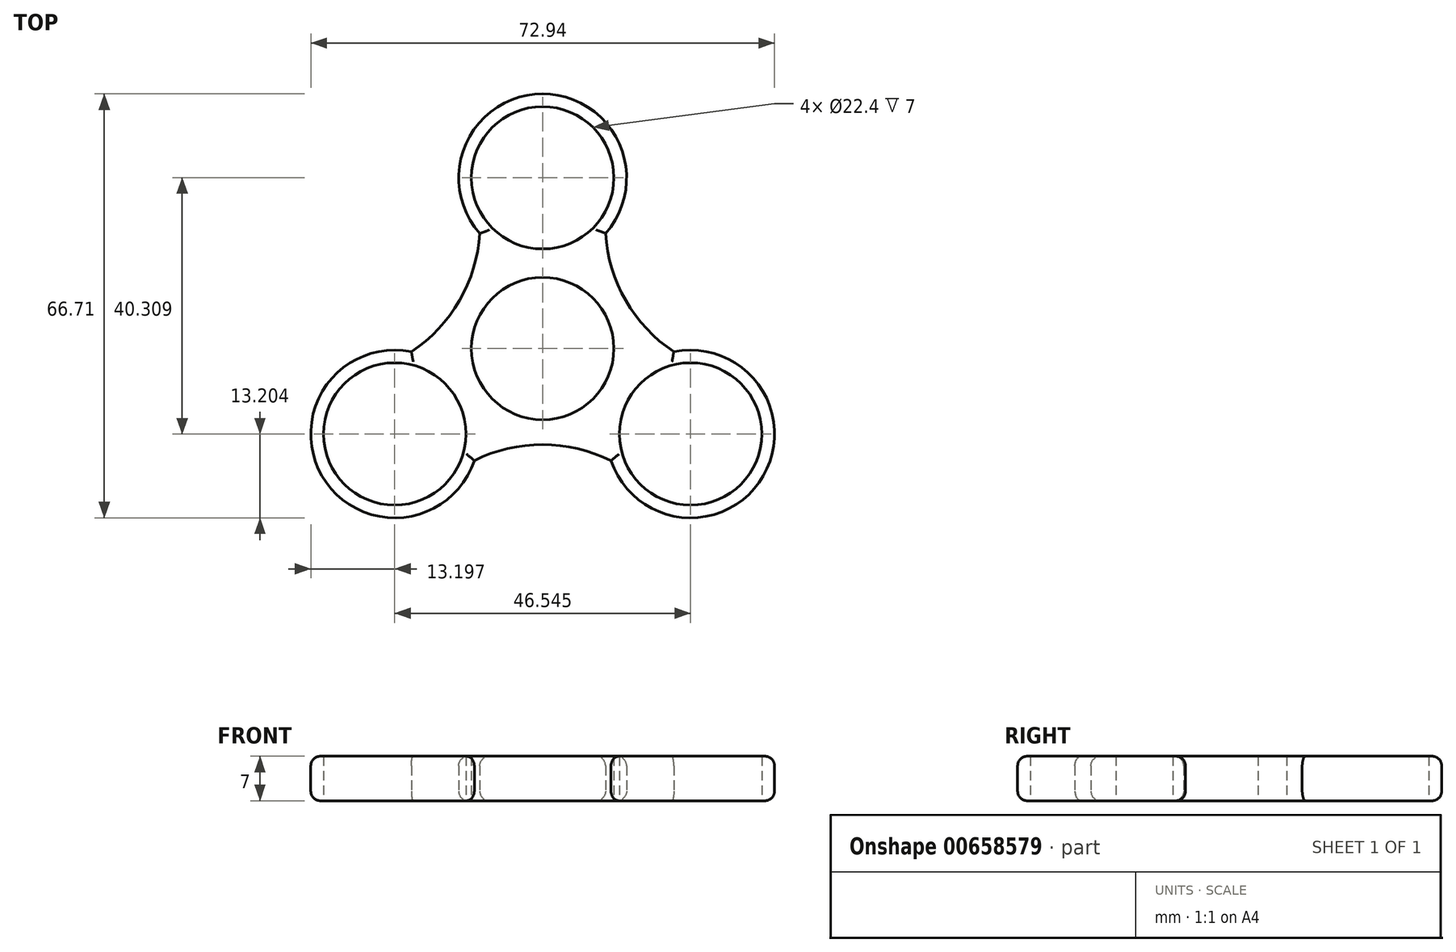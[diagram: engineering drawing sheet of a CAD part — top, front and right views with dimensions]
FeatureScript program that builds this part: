
annotation { "Feature Type Name" : "Feature", "Feature Type Description" : "" }
export const myFeature = defineFeature(function(context is Context, id is Id, definition is map)
    precondition{}
    {
        {
            var Q0;
            Q0=qCreatedBy(makeId("Top.planeOp"),FACE);
            var sketch = newSketch(context, id + "F0", { "sketchPlane" : qUnion([Q0])});
            skCircle(sketch, "E0", {"center": v(0, 0) * mm, "radius": 11.2 * mm});
            skCircle(sketch, "E1", {"center": v(0, 26.87) * mm, "radius": 11.2 * mm});
            skArc(sketch, "E2", {"start": v(9.9, 18.13) * mm, "mid": v(0, 40.07) * mm, "end": v(-9.88, 18.12) * mm});
            skArc(sketch, "E3.1.0", {"start": v(-20.65, -0.5) * mm, "mid": v(-34.7, -20.04) * mm, "end": v(-10.75, -17.62) * mm});
            skCircle(sketch, "E3.1.1", {"center": v(-23.27, -13.44) * mm, "radius": 11.2 * mm});
            skArc(sketch, "E3.2.0", {"start": v(10.76, -17.64) * mm, "mid": v(34.7, -20.03) * mm, "end": v(20.64, -0.5) * mm});
            skCircle(sketch, "E3.2.1", {"center": v(23.27, -13.44) * mm, "radius": 11.2 * mm});
            skArc(sketch, "E4", {"start": v(9.9, 18.13) * mm, "mid": v(13.08, 7.56) * mm, "end": v(20.64, -0.5) * mm});
            skArc(sketch, "E5.1.0", {"start": v(-20.65, -0.5) * mm, "mid": v(-13.08, 7.55) * mm, "end": v(-9.88, 18.12) * mm});
            skArc(sketch, "E5.2.0", {"start": v(10.76, -17.64) * mm, "mid": v(0, -15.1) * mm, "end": v(-10.75, -17.62) * mm});
            skSolve(sketch);
        }
        {
            var Q0;
            Q0=makeQuery(id+"F0.imprint","IMPRINT",FACE,{"disambiguationData":[TD([[makeQuery(id+"F0.imprint","IMPRINT",EDGE,{"derivedFrom":sQuery(id+"F0.wireOp",EDGE,"E0")}),-1.0]])]});
            extrude(context, id + "F1", {"entities" : qUnion([Q0]), "depth" : 7 * mm, "offsetDistance" : 25 * mm});
        }
        {
            var Q0;
            Q0=makeQuery(id+"F1.opExtrude","CAP_EDGE",EDGE,{"disambiguationData":[OSD([sQuery(id+"F0.wireOp",EDGE,"E3.1.0")])],"isStart":false});
            var Q1;
            Q1=makeQuery(id+"F1.opExtrude","CAP_EDGE",EDGE,{"disambiguationData":[OSD([sQuery(id+"F0.wireOp",EDGE,"E5.1.0")])],"isStart":false});
            var Q2;
            Q2=makeQuery(id+"F1.opExtrude","CAP_EDGE",EDGE,{"disambiguationData":[OSD([sQuery(id+"F0.wireOp",EDGE,"E4")])],"isStart":false});
            var Q3;
            Q3=makeQuery(id+"F1.opExtrude","CAP_EDGE",EDGE,{"disambiguationData":[OSD([sQuery(id+"F0.wireOp",EDGE,"E5.2.0")])],"isStart":false});
            var Q4;
            Q4=makeQuery(id+"F1.opExtrude","CAP_EDGE",EDGE,{"disambiguationData":[OSD([sQuery(id+"F0.wireOp",EDGE,"E3.2.0")])],"isStart":false});
            var Q5;
            Q5=makeQuery(id+"F1.opExtrude","CAP_EDGE",EDGE,{"disambiguationData":[OSD([sQuery(id+"F0.wireOp",EDGE,"E2")])],"isStart":false});
            var Q6;
            Q6=makeQuery(id+"F1.opExtrude","CAP_EDGE",EDGE,{"disambiguationData":[OSD([sQuery(id+"F0.wireOp",EDGE,"E5.2.0")])],"isStart":true});
            fillet(context, id + "F2", {"entities" : qUnion([Q0, Q1, Q2, Q3, Q4, Q5, Q6]), "radius" : 1.5 * mm, "tangentPropagation" : true, "allowEdgeOverflow" : false});
        }
        {
            var Q0;
            {var subQ0=sQuery(id+"F0.wireOp",EDGE,"E5.2.0");Q0=makeQuery(id+"F2.opFillet","BLEND_EDGE",EDGE,{"blendedFrom":[makeQuery(id+"F1.opExtrude","CAP_EDGE",EDGE,{"disambiguationData":[OSD([subQ0])],"isStart":true}),makeQuery(id+"F1.opExtrude","CAP_FACE",FACE,{"disambiguationData":[OSD([sQuery(id+"F0.wireOp",EDGE,"E0"),sQuery(id+"F0.wireOp",EDGE,"E1"),sQuery(id+"F0.wireOp",EDGE,"E2"),sQuery(id+"F0.wireOp",EDGE,"E3.1.0"),sQuery(id+"F0.wireOp",EDGE,"E3.1.1"),sQuery(id+"F0.wireOp",EDGE,"E3.2.0"),sQuery(id+"F0.wireOp",EDGE,"E3.2.1"),sQuery(id+"F0.wireOp",EDGE,"E4"),sQuery(id+"F0.wireOp",EDGE,"E5.1.0"),subQ0])],"isStart":true})],"blendedInto":[makeQuery(id+"F1.opExtrude","CAP_FACE",FACE,{"disambiguationData":[OSD([sQuery(id+"F0.wireOp",EDGE,"E0"),sQuery(id+"F0.wireOp",EDGE,"E1"),sQuery(id+"F0.wireOp",EDGE,"E2"),sQuery(id+"F0.wireOp",EDGE,"E3.1.0"),sQuery(id+"F0.wireOp",EDGE,"E3.1.1"),sQuery(id+"F0.wireOp",EDGE,"E3.2.0"),sQuery(id+"F0.wireOp",EDGE,"E3.2.1"),sQuery(id+"F0.wireOp",EDGE,"E4"),sQuery(id+"F0.wireOp",EDGE,"E5.1.0"),subQ0])],"isStart":true})]});}
            var Q1;
            Q1=makeQuery(id+"F1.opExtrude","CAP_EDGE",EDGE,{"disambiguationData":[OSD([sQuery(id+"F0.wireOp",EDGE,"E4")])],"isStart":true});
            var Q2;
            Q2=makeQuery(id+"F1.opExtrude","CAP_EDGE",EDGE,{"disambiguationData":[OSD([sQuery(id+"F0.wireOp",EDGE,"E2")])],"isStart":true});
            var Q3;
            Q3=makeQuery(id+"F1.opExtrude","CAP_EDGE",EDGE,{"disambiguationData":[OSD([sQuery(id+"F0.wireOp",EDGE,"E3.1.0")])],"isStart":true});
            var Q4;
            Q4=makeQuery(id+"F1.opExtrude","CAP_EDGE",EDGE,{"disambiguationData":[OSD([sQuery(id+"F0.wireOp",EDGE,"E5.1.0")])],"isStart":true});
            var Q5;
            Q5=makeQuery(id+"F1.opExtrude","CAP_EDGE",EDGE,{"disambiguationData":[OSD([sQuery(id+"F0.wireOp",EDGE,"E3.2.0")])],"isStart":true});
            fillet(context, id + "F3", {"entities" : qUnion([Q0, Q1, Q2, Q3, Q4, Q5]), "radius" : 1.5 * mm, "tangentPropagation" : true, "allowEdgeOverflow" : false});
        }
    });
